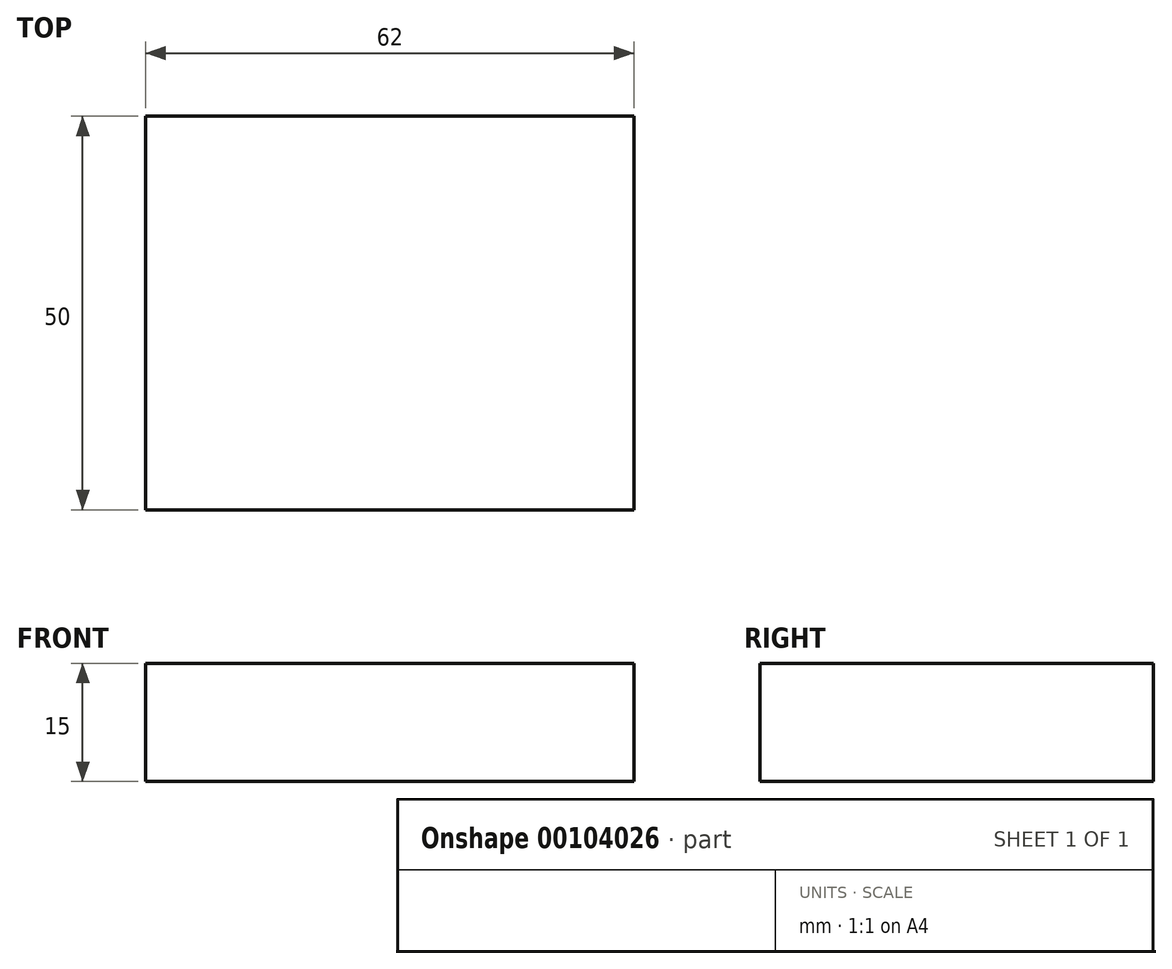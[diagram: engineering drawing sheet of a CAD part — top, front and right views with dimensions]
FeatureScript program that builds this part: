
annotation { "Feature Type Name" : "Feature", "Feature Type Description" : "" }
export const myFeature = defineFeature(function(context is Context, id is Id, definition is map)
    precondition{}
    {
        {
            var Q0;
            Q0=qCreatedBy(makeId("Top.planeOp"),FACE);
            var sketch = newSketch(context, id + "F0", { "sketchPlane" : qUnion([Q0])});
            skLineSegment(sketch, "E0.bottom", {"start": v(-104.08, 23.16) * mm, "end": v(-42.08, 23.16) * mm});
            skLineSegment(sketch, "E0.top", {"start": v(-104.08, -26.84) * mm, "end": v(-42.08, -26.84) * mm});
            skLineSegment(sketch, "E0.left", {"start": v(-104.08, 23.16) * mm, "end": v(-104.08, -26.84) * mm});
            skLineSegment(sketch, "E0.right", {"start": v(-42.08, 23.16) * mm, "end": v(-42.08, -26.84) * mm});
            skSolve(sketch);
        }
        {
            var Q0;
            Q0 = qSketchRegion(id + "F0", true);
            extrude(context, id + "F1", {"entities" : qUnion([Q0]), "depth" : 15 * mm, "offsetDistance" : 25 * mm});
        }
    });
